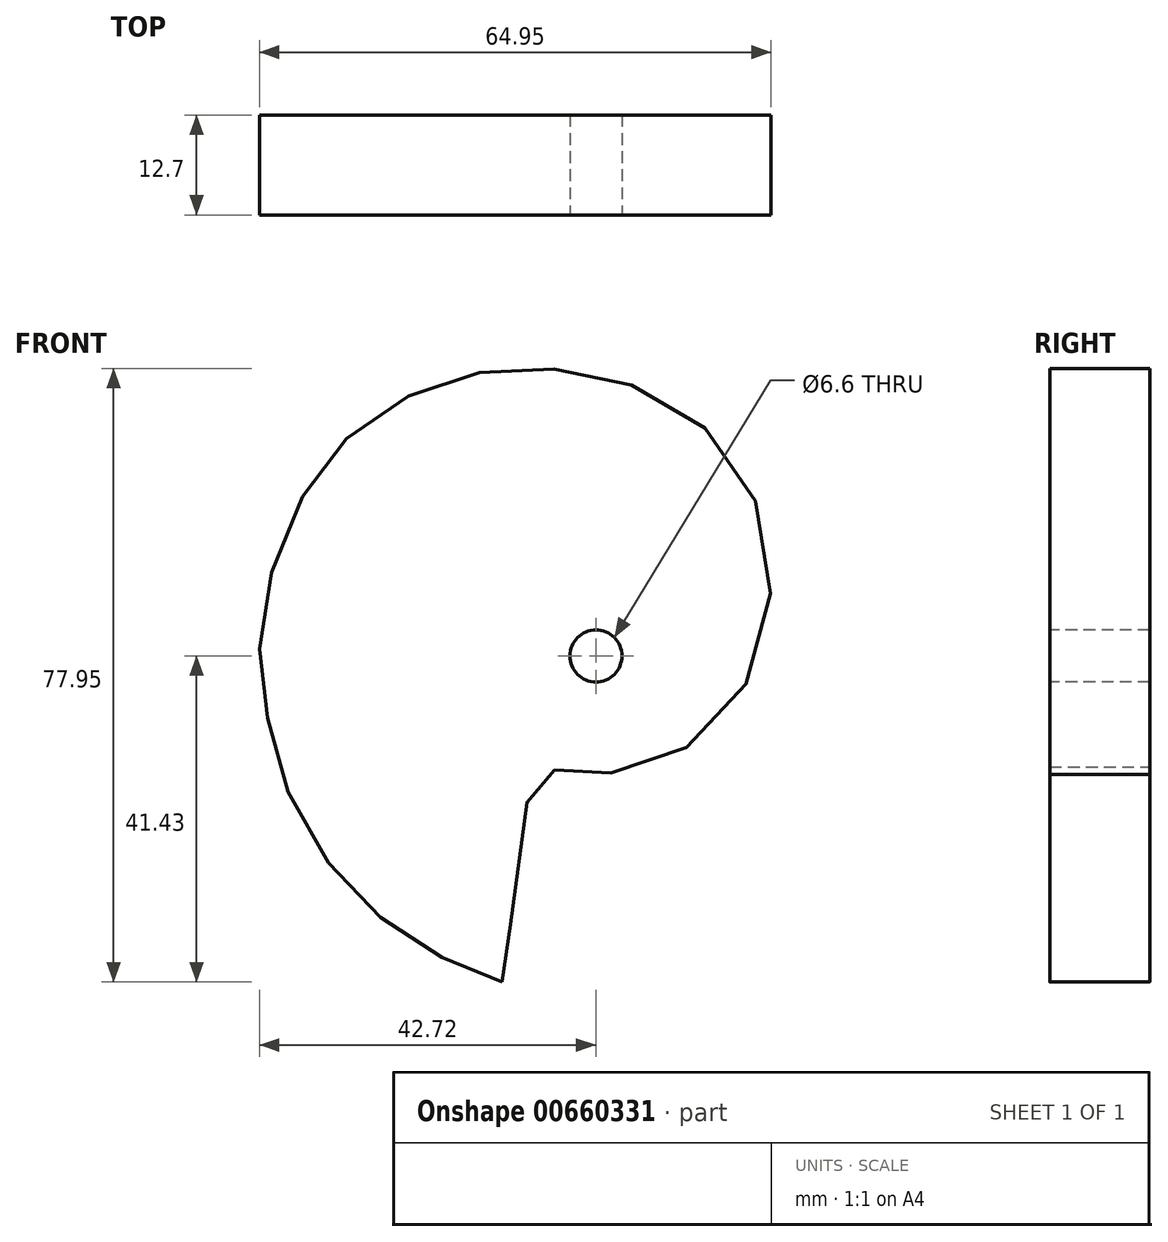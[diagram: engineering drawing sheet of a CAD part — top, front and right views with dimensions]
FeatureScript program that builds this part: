
annotation { "Feature Type Name" : "Feature", "Feature Type Description" : "" }
export const myFeature = defineFeature(function(context is Context, id is Id, definition is map)
    precondition{}
    {
        {
            var Q0;
            Q0=qCreatedBy(makeId("Front.planeOp"),FACE);
            var sketch = newSketch(context, id + "F0", { "sketchPlane" : qUnion([Q0])});
            skFitSpline(sketch, "E0", {"points": [v(-11.9, -41.42) * mm, v(-21.05, -37.46) * mm, v(-30.11, -30.71) * mm, v(-38.33, -19.12) * mm, v(-41.91, -6.69) * mm, v(-42.55, 4.06) * mm, v(-38.33, 18.18) * mm, v(-31.37, 27.88) * mm, v(-20.63, 34.41) * mm, v(-8.82, 36.52) * mm, v(4.45, 34.41) * mm, v(17.31, 25.14) * mm, v(22.16, 7.22) * mm, v(14.78, -9.22) * mm, v(1.71, -14.9) * mm, v(-5.24, -14.48) * mm, v(-7.35, -14.48) * mm, v(-11.14, -38.51) * mm, v(-11.9, -41.42) * mm]});
            skSolve(sketch);
        }
        {
            var Q0;
            Q0=makeQuery(id+"F0.imprint","IMPRINT",FACE,{"disambiguationData":[TD([[makeQuery(id+"F0.imprint","IMPRINT",EDGE,{"derivedFrom":sQuery(id+"F0.wireOp",EDGE,"E0")}),-1.0]])]});
            var Q1;
            Q1=sQuery(id+"F0.wireOp",EDGE,"E0");
            extrude(context, id + "F1", {"entities" : qUnion([Q0]), "surfaceEntities" : qUnion([Q1]), "depth" : 12.7 * mm, "offsetDistance" : 25.4 * mm});
        }
        {
            var Q0;
            Q0=makeQuery(id+"F1.opExtrude","CAP_FACE",FACE,{"disambiguationData":[OSD([sQuery(id+"F0.wireOp",EDGE,"E0")])],"isStart":false});
            var sketch = newSketch(context, id + "F2", { "sketchPlane" : qUnion([Q0])});
            skCircle(sketch, "E1", {"center": v(0, 0) * mm, "radius": 3.3 * mm});
            skSolve(sketch);
        }
        {
            var Q0;
            Q0 = qSketchRegion(id + "F2", true);
            extrude(context, id + "F3", {"entities" : qUnion([Q0]), "operationType" : NewBodyOperationType.REMOVE, "oppositeDirection" : true, "depth" : 25.4 * mm, "offsetDistance" : 25.4 * mm});
        }
    });
